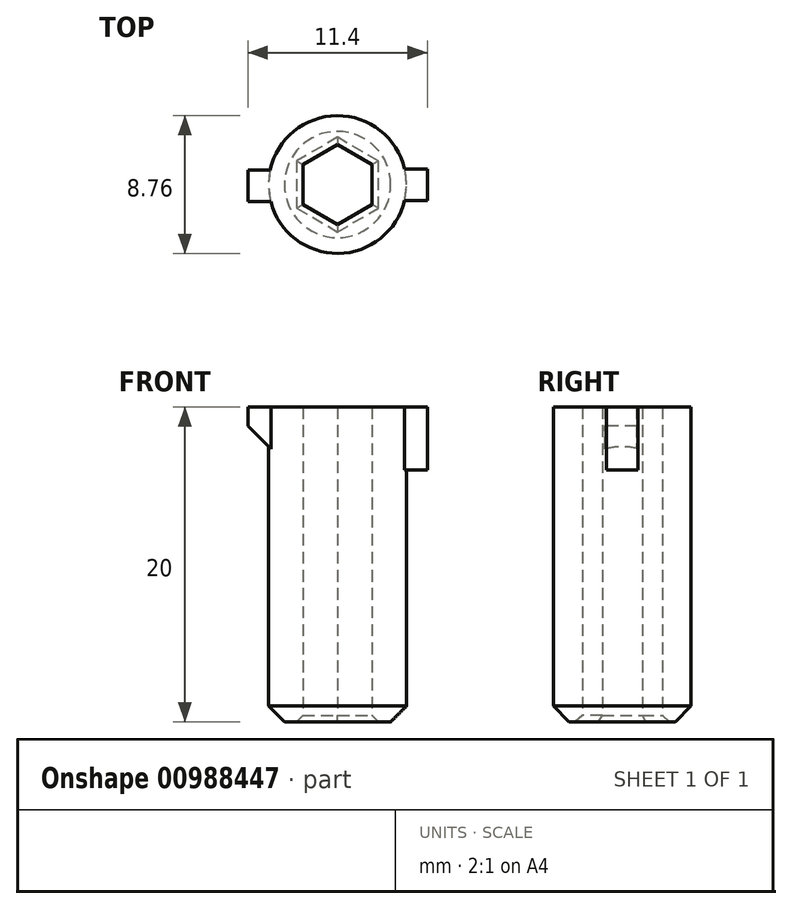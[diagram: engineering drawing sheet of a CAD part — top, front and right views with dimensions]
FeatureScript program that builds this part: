
annotation { "Feature Type Name" : "Feature", "Feature Type Description" : "" }
export const myFeature = defineFeature(function(context is Context, id is Id, definition is map)
    precondition{}
    {
        {
            var Q0;
            Q0=qCreatedBy(makeId("Top.planeOp"),FACE);
            var sketch = newSketch(context, id + "F0", { "sketchPlane" : qUnion([Q0])});
            skPoint(sketch, "E0", {"position": v(0, 0) * mm});
            skCircle(sketch, "E1", {"center": v(0, 0) * mm, "radius": 4.38 * mm});
            skCircle(sketch, "E2.cCircle", {"center": v(0, 0) * mm, "radius": 2.54 * mm, "construction": true});
            skLineSegment(sketch, "E2.0", {"start": v(-2.2, 1.27) * mm, "end": v(0, 2.54) * mm});
            skLineSegment(sketch, "E2.1", {"start": v(0, 2.54) * mm, "end": v(2.2, 1.27) * mm});
            skLineSegment(sketch, "E2.2", {"start": v(2.2, 1.27) * mm, "end": v(2.2, -1.27) * mm});
            skLineSegment(sketch, "E2.3", {"start": v(2.2, -1.27) * mm, "end": v(0, -2.54) * mm});
            skLineSegment(sketch, "E2.4", {"start": v(0, -2.54) * mm, "end": v(-2.2, -1.27) * mm});
            skLineSegment(sketch, "E2.5", {"start": v(-2.2, -1.27) * mm, "end": v(-2.2, 1.27) * mm});
            skSolve(sketch);
        }
        {
            var Q0;
            Q0 = qSketchRegion(id + "F0", true);
            extrude(context, id + "F1", {"entities" : qUnion([Q0]), "depth" : 20 * mm, "offsetDistance" : 25 * mm});
        }
        {
            var Q0;
            Q0=makeQuery(id+"F1.opExtrude","SWEPT_FACE",FACE,{"disambiguationData":[OSD([sQuery(id+"F0.wireOp",EDGE,"E2.5")])]});
            var sketch = newSketch(context, id + "F2", { "sketchPlane" : qUnion([Q0])});
            skLineSegment(sketch, "E3.bottom", {"start": v(0.91, 20) * mm, "end": v(-1.09, 20) * mm});
            skLineSegment(sketch, "E3.top", {"start": v(0.91, 16) * mm, "end": v(-1.09, 16) * mm});
            skLineSegment(sketch, "E3.left", {"start": v(0.91, 20) * mm, "end": v(0.91, 16) * mm});
            skLineSegment(sketch, "E3.right", {"start": v(-1.09, 20) * mm, "end": v(-1.09, 16) * mm});
            skSolve(sketch);
        }
        {
            var Q0;
            Q0 = qSketchRegion(id + "F2", true);
            extrude(context, id + "F3", {"entities" : qUnion([Q0]), "operationType" : NewBodyOperationType.ADD, "oppositeDirection" : true, "depth" : 3.5 * mm, "offsetDistance" : 25 * mm});
        }
        {
            var Q0;
            Q0=makeQuery(id+"F1.opExtrude","SWEPT_FACE",FACE,{"disambiguationData":[OSD([sQuery(id+"F0.wireOp",EDGE,"E2.2")])]});
            var sketch = newSketch(context, id + "F4", { "sketchPlane" : qUnion([Q0])});
            skLineSegment(sketch, "E4.bottom", {"start": v(1.01, 20) * mm, "end": v(-0.99, 20) * mm});
            skLineSegment(sketch, "E4.top", {"start": v(1.01, 16) * mm, "end": v(-0.99, 16) * mm});
            skLineSegment(sketch, "E4.left", {"start": v(1.01, 20) * mm, "end": v(1.01, 16) * mm});
            skLineSegment(sketch, "E4.right", {"start": v(-0.99, 20) * mm, "end": v(-0.99, 16) * mm});
            skSolve(sketch);
        }
        {
            var Q0;
            Q0 = qSketchRegion(id + "F4", true);
            extrude(context, id + "F5", {"entities" : qUnion([Q0]), "operationType" : NewBodyOperationType.ADD, "oppositeDirection" : true, "depth" : 3.5 * mm, "offsetDistance" : 25 * mm});
        }
        {
            var Q0;
            Q0=makeQuery(id+"F3.opExtrude","CAP_EDGE",EDGE,{"disambiguationData":[OSD([sQuery(id+"F2.wireOp",EDGE,"E3.top")])],"isStart":false});
            chamfer(context, id + "F6", {"entities" : qUnion([Q0]), "width" : 2.8 * mm, "tangentPropagation" : true});
        }
        {
            var Q0;
            Q0=makeQuery(id+"F1.opExtrude","CAP_EDGE",EDGE,{"disambiguationData":[OSD([sQuery(id+"F0.wireOp",EDGE,"E1")])],"isStart":true});
            chamfer(context, id + "F7", {"entities" : qUnion([Q0]), "width" : 1 * mm, "tangentPropagation" : true});
        }
        {
            var Q0;
            Q0=makeQuery(id+"F1.opExtrude","CAP_EDGE",EDGE,{"disambiguationData":[OSD([sQuery(id+"F0.wireOp",EDGE,"E2.2")])],"isStart":true});
            var Q1;
            Q1=makeQuery(id+"F1.opExtrude","CAP_EDGE",EDGE,{"disambiguationData":[OSD([sQuery(id+"F0.wireOp",EDGE,"E2.3")])],"isStart":true});
            var Q2;
            Q2=makeQuery(id+"F1.opExtrude","CAP_EDGE",EDGE,{"disambiguationData":[OSD([sQuery(id+"F0.wireOp",EDGE,"E2.4")])],"isStart":true});
            var Q3;
            Q3=makeQuery(id+"F1.opExtrude","CAP_EDGE",EDGE,{"disambiguationData":[OSD([sQuery(id+"F0.wireOp",EDGE,"E2.5")])],"isStart":true});
            var Q4;
            Q4=makeQuery(id+"F1.opExtrude","CAP_EDGE",EDGE,{"disambiguationData":[OSD([sQuery(id+"F0.wireOp",EDGE,"E2.0")])],"isStart":true});
            var Q5;
            Q5=makeQuery(id+"F1.opExtrude","CAP_EDGE",EDGE,{"disambiguationData":[OSD([sQuery(id+"F0.wireOp",EDGE,"E2.1")])],"isStart":true});
            chamfer(context, id + "F8", {"entities" : qUnion([Q0, Q1, Q2, Q3, Q4, Q5]), "width" : 0.4 * mm, "tangentPropagation" : true});
        }
    });
